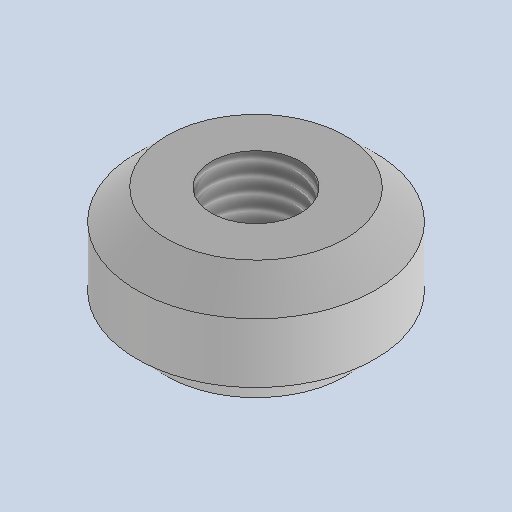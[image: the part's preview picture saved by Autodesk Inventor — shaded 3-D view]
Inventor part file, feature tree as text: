
AUTODESK INVENTOR PART (.ipt)
format: ipt  version: 2024 (Build 280153000, 153)  size: 155,136 bytes
history: native  units: mm
features: other x4, reference x2, extrude x1, thread x1, chamfer x1, sketch x1
ambient origin geometry x8: Origin, YZ Plane, XZ Plane, XY Plane, X Axis, Y Axis, Z Axis, Center Point
bodies: Solid1 (feature_tree)
feature tree (10):
  extrude  "Extrusion1"  Depth=4.0mm TaperAngle=0.0deg
  thread  "Thread1"  [1 undecoded]
  chamfer  "Chamfer1"  Distance=1.0mm Angle=45.0deg
  sketch  "Sketch1"  dims[d0=2.99986mm d1=4.0mm d2=0.0mm d3=4.0mm d4=0.0mm d5=1.0mm d6=2.0mm d7=45.0deg]
  reference  "Reference1"
  reference  "Reference2"
  other  "<userpath> windows\Documents\Inventor\Robotska_roka\roka_asemb.iam"
  other  "roka_asemb.iam"
  other  "sornik1:1"
  other  "povezava:4"
note: 1 required parameter value undecoded (feature->parameter linkage not recoverable at this tier; creation-order binding heuristic only, values carry confidence <= 0.55)
